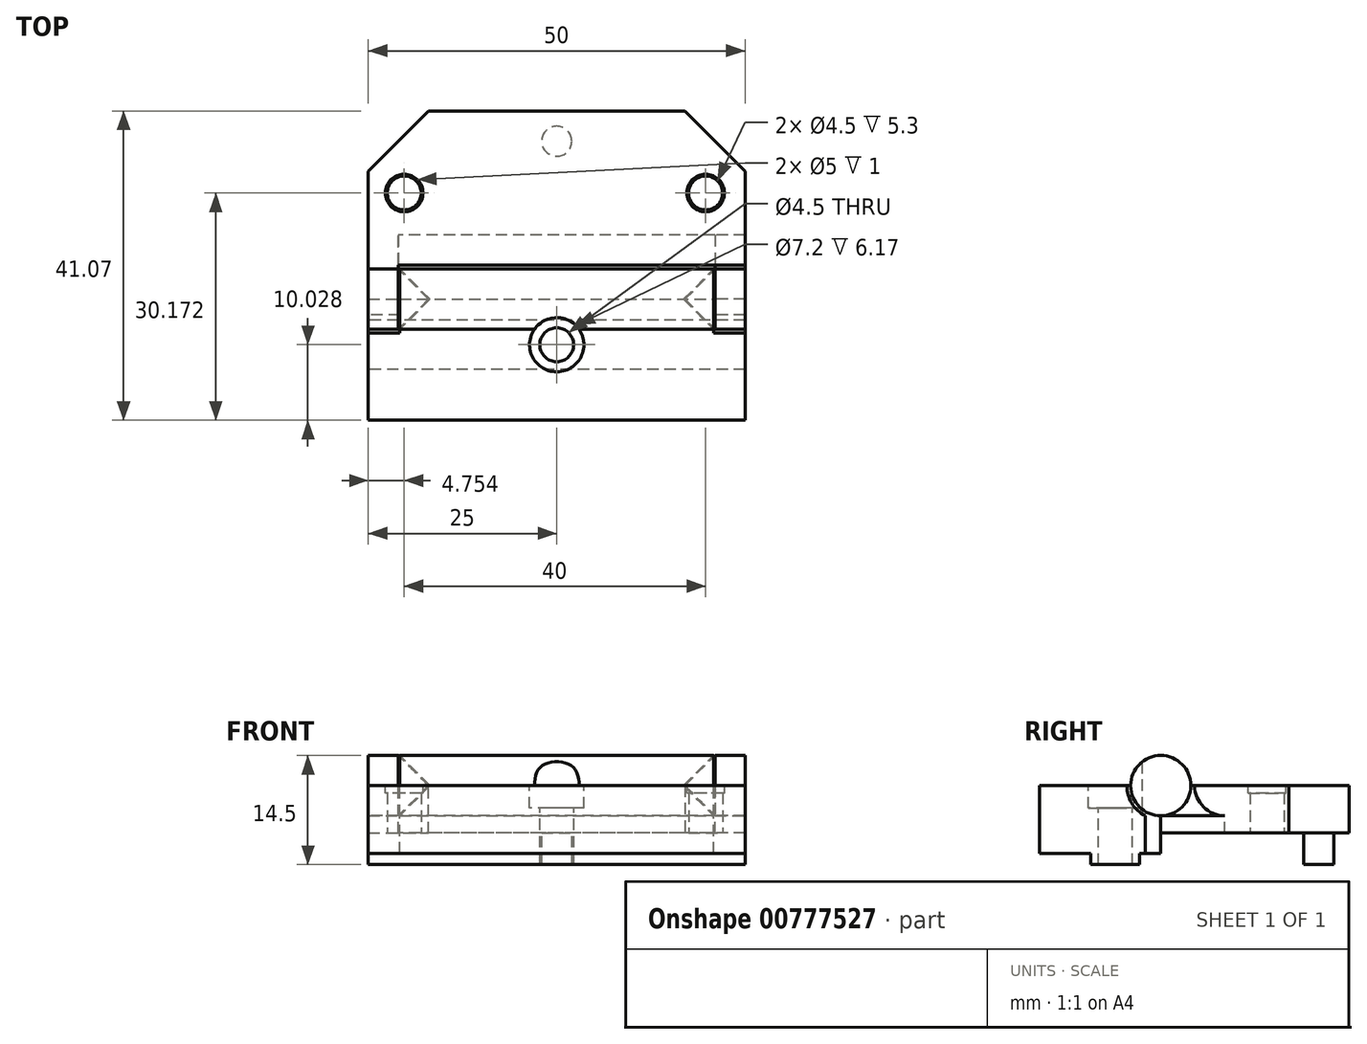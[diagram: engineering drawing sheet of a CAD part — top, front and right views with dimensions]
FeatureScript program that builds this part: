
annotation { "Feature Type Name" : "Feature", "Feature Type Description" : "" }
export const myFeature = defineFeature(function(context is Context, id is Id, definition is map)
    precondition{}
    {
        {
            var Q0;
            Q0=qCreatedBy(makeId("Top.planeOp"),FACE);
            var sketch = newSketch(context, id + "F0", { "sketchPlane" : qUnion([Q0])});
            skLineSegment(sketch, "E0", {"start": v(0, 0) * mm, "end": v(-16.82, 0) * mm});
            skLineSegment(sketch, "E1", {"start": v(-16.82, 0) * mm, "end": v(-20.82, 4) * mm});
            skLineSegment(sketch, "E2", {"start": v(-20.82, 4) * mm, "end": v(0, 4) * mm});
            skLineSegment(sketch, "E3", {"start": v(0, 4) * mm, "end": v(0, 0) * mm});
            skLineSegment(sketch, "E4", {"start": v(-17, 0) * mm, "end": v(-21, 4) * mm});
            skLineSegment(sketch, "E5", {"start": v(-21, 4) * mm, "end": v(-25, 4) * mm});
            skLineSegment(sketch, "E6", {"start": v(-25, 4) * mm, "end": v(-25, 0) * mm});
            skLineSegment(sketch, "E7", {"start": v(-25, 0) * mm, "end": v(-17, 0) * mm});
            skLineSegment(sketch, "E8.MirrorCS", {"start": v(21, 4) * mm, "end": v(25, 4) * mm});
            skLineSegment(sketch, "E9.MirrorCS", {"start": v(17, 0) * mm, "end": v(21, 4) * mm});
            skLineSegment(sketch, "E10.MirrorCS", {"start": v(25, 0) * mm, "end": v(17, 0) * mm});
            skLineSegment(sketch, "E11.MirrorCS", {"start": v(25, 4) * mm, "end": v(25, 0) * mm});
            skLineSegment(sketch, "E12.MirrorCS", {"start": v(16.82, 0) * mm, "end": v(20.82, 4) * mm});
            skLineSegment(sketch, "E13.MirrorCS", {"start": v(20.82, 4) * mm, "end": v(0, 4) * mm});
            skLineSegment(sketch, "E14.MirrorCS", {"start": v(0, 0) * mm, "end": v(16.82, 0) * mm});
            skSolve(sketch);
        }
        {
            var Q0;
            Q0=makeQuery(id+"F0.imprint","IMPRINT",FACE,{"disambiguationData":[TD([[makeQuery(id+"F0.imprint","IMPRINT",EDGE,{"derivedFrom":sQuery(id+"F0.wireOp",EDGE,"E4")}),1.0]])]});
            var Q1;
            Q1=makeQuery(id+"F0.imprint","IMPRINT",FACE,{"disambiguationData":[TD([[makeQuery(id+"F0.imprint","IMPRINT",EDGE,{"derivedFrom":sQuery(id+"F0.wireOp",EDGE,"E0")}),-1.0]])]});
            var Q2;
            Q2=makeQuery(id+"F0.imprint","IMPRINT",FACE,{"disambiguationData":[TD([[makeQuery(id+"F0.imprint","IMPRINT",EDGE,{"derivedFrom":sQuery(id+"F0.wireOp",EDGE,"E3")}),1.0]])]});
            var Q3;
            Q3=makeQuery(id+"F0.imprint","IMPRINT",FACE,{"disambiguationData":[TD([[makeQuery(id+"F0.imprint","IMPRINT",EDGE,{"derivedFrom":sQuery(id+"F0.wireOp",EDGE,"E8.MirrorCS")}),-1.0]])]});
            var Q4;
            Q4=sQuery(id+"F0.wireOp",EDGE,"E0");
            revolve(context, id + "F1", {"entities" : qUnion([Q0, Q1, Q2, Q3]), "axis" : qUnion([Q4]), "revolveType" : RevolveType.FULL});
        }
        {
            var Q0;
            Q0=qCreatedBy(makeId("Front.planeOp"),FACE);
            cPlane(context, id + "F2", {"entities" : qUnion([Q0]), "cplaneType" : CPlaneType.OFFSET, "offset" : 25 * mm, "width" : 150 * mm, "height" : 150 * mm});
        }
        {
            var Q0;
            Q0=qCreatedBy(makeId("Front.planeOp"),FACE);
            cPlane(context, id + "F3", {"entities" : qUnion([Q0]), "cplaneType" : CPlaneType.OFFSET, "offset" : 25 * mm, "oppositeDirection" : true, "width" : 150 * mm, "height" : 150 * mm});
        }
        {
            var Q0;
            Q0=qCreatedBy(id+"F2.planeOp",FACE);
            var sketch = newSketch(context, id + "F4", { "sketchPlane" : qUnion([Q0])});
            skLineSegment(sketch, "E15", {"start": v(20.82, -4) * mm, "end": v(-20.82, -4) * mm});
            skLineSegment(sketch, "E16", {"start": v(-20.82, 4) * mm, "end": v(20.82, 4) * mm});
            skLineSegment(sketch, "E17.0", {"start": v(-20.82, 4) * mm, "end": v(-20.82, -4) * mm});
            skLineSegment(sketch, "E18.0", {"start": v(20.82, 4) * mm, "end": v(20.82, -4) * mm});
            skSolve(sketch);
        }
        {
            var Q0;
            Q0=qSketchRegion(id+"F4",true);
            var Q1;
            Q1=makeQuery(id+"F1.opRevolve","SWEPT_FACE",FACE,{"disambiguationData":[OSD([sQuery(id+"F0.wireOp",EDGE,"E2"),sQuery(id+"F0.wireOp",EDGE,"E13.MirrorCS")])]});
            extrude(context, id + "F5", {"entities" : qUnion([Q0]), "operationType" : NewBodyOperationType.ADD, "endBound" : BoundingType.UP_TO_SURFACE, "oppositeDirection" : true, "endBoundEntityFace" : qUnion([Q1]), "depth" : 25 * mm});
        }
        {
            var Q0;
            Q0=qCreatedBy(id+"F3.planeOp",FACE);
            var sketch = newSketch(context, id + "F6", { "sketchPlane" : qUnion([Q0])});
            skLineSegment(sketch, "E19", {"start": v(25, -4) * mm, "end": v(21, -4) * mm});
            skLineSegment(sketch, "E20", {"start": v(21, 4) * mm, "end": v(25, 4) * mm});
            skLineSegment(sketch, "E21", {"start": v(-21, -4) * mm, "end": v(-25, -4) * mm});
            skLineSegment(sketch, "E22", {"start": v(-25, 4) * mm, "end": v(-21, 4) * mm});
            skLineSegment(sketch, "E23.0", {"start": v(-21, 4) * mm, "end": v(-21, -4) * mm});
            skLineSegment(sketch, "E24.0", {"start": v(-25, 4) * mm, "end": v(-25, -4) * mm});
            skLineSegment(sketch, "E25.0", {"start": v(21, 4) * mm, "end": v(21, -4) * mm});
            skLineSegment(sketch, "E26.0", {"start": v(25, 4) * mm, "end": v(25, -4) * mm});
            skSolve(sketch);
        }
        {
            var Q0;
            Q0=makeQuery(id+"F6.imprint","IMPRINT",FACE,{"disambiguationData":[TD([[makeQuery(id+"F6.imprint","IMPRINT",EDGE,{"derivedFrom":sQuery(id+"F6.wireOp",EDGE,"E19")}),-1.0]])]});
            var Q1;
            Q1=makeQuery(id+"F6.imprint","IMPRINT",FACE,{"disambiguationData":[TD([[makeQuery(id+"F6.imprint","IMPRINT",EDGE,{"derivedFrom":sQuery(id+"F6.wireOp",EDGE,"E21")}),-1.0]])]});
            extrude(context, id + "F7", {"entities" : qUnion([Q0, Q1]), "operationType" : NewBodyOperationType.ADD, "endBound" : BoundingType.UP_TO_NEXT, "depth" : 25 * mm, "offsetDistance" : 25 * mm});
        }
        {
            var Q0;
            Q0=makeQuery(id+"F7.opExtrude","SWEPT_FACE",FACE,{"disambiguationData":[OSD([sQuery(id+"F6.wireOp",EDGE,"E23.0")])]});
            var Q1;
            Q1=makeQuery(id+"F7.opExtrude","SWEPT_FACE",FACE,{"disambiguationData":[OSD([sQuery(id+"F6.wireOp",EDGE,"E25.0")])]});
            var Q2;
            Q2=makeQuery(id+"F1.opRevolve","SWEPT_BODY",BODY,{"disambiguationData":[OSD([sQuery(id+"F0.wireOp",EDGE,"E8.MirrorCS"),sQuery(id+"F0.wireOp",EDGE,"E9.MirrorCS"),sQuery(id+"F0.wireOp",EDGE,"E11.MirrorCS"),sQuery(id+"F0.wireOp",EDGE,"E10.MirrorCS")])]});
            extrude(context, id + "F8", {"entities" : qUnion([Q0]), "endBound" : BoundingType.UP_TO_SURFACE, "depth" : 6 * mm, "endBoundEntityFace" : qUnion([Q1]), "endBoundEntityBody" : qUnion([Q2]), "offsetDistance" : 25 * mm});
        }
        {
            var Q0;
            Q0=makeQuery(id+"F8.opExtrude","CAP_FACE",FACE,{"disambiguationData":[OSD([sQuery(id+"F6.wireOp",EDGE,"E23.0")])],"isStart":true});
            var sketch = newSketch(context, id + "F9", { "sketchPlane" : qUnion([Q0])});
            skArc(sketch, "E27.0", {"start": v(0, -4) * mm, "mid": v(-4, 0) * mm, "end": v(0, 4) * mm});
            skLineSegment(sketch, "E28", {"start": v(-4.25, 4) * mm, "end": v(-4.25, -4) * mm, "construction": true});
            skArc(sketch, "E29.MirrorCS", {"start": v(-8.5, -4) * mm, "mid": v(-4.5, 0) * mm, "end": v(-8.5, 4) * mm});
            skSolve(sketch);
        }
        {
            var Q0;
            {var subQ0=sQuery(id+"F9.wireOp",EDGE,"E27.0");Q0=makeQuery(id+"F9.imprint","IMPRINT",FACE,{"disambiguationData":[TD([[makeQuery(id+"F9.imprint","IMPRINT",EDGE,{"derivedFrom":subQ0}),1.0]])]});}
            extrude(context, id + "F10", {"entities" : qUnion([Q0]), "operationType" : NewBodyOperationType.REMOVE, "endBound" : BoundingType.THROUGH_ALL, "oppositeDirection" : true, "depth" : 25 * mm, "offsetDistance" : 25 * mm});
        }
        {
            var Q0;
            Q0=makeQuery(id+"F7.opExtrude","SWEPT_FACE",FACE,{"disambiguationData":[OSD([sQuery(id+"F6.wireOp",EDGE,"E23.0")])]});
            var sketch = newSketch(context, id + "F11", { "sketchPlane" : qUnion([Q0])});
            skLineSegment(sketch, "E30", {"start": v(25, 0) * mm, "end": v(4, 0) * mm});
            skSolve(sketch);
        }
        {
            var Q0;
            Q0=makeQuery(id+"F1.opRevolve","SWEPT_BODY",BODY,{"disambiguationData":[OSD([sQuery(id+"F0.wireOp",EDGE,"E8.MirrorCS"),sQuery(id+"F0.wireOp",EDGE,"E9.MirrorCS"),sQuery(id+"F0.wireOp",EDGE,"E11.MirrorCS"),sQuery(id+"F0.wireOp",EDGE,"E10.MirrorCS")])]});
            var Q1;
            Q1=makeQuery(id+"F8.opExtrude","SWEPT_BODY",BODY,{"disambiguationData":[OSD([sQuery(id+"F6.wireOp",EDGE,"E23.0")])]});
            var Q2;
            Q2=makeQuery(id+"F1.opRevolve","SWEPT_BODY",BODY,{"disambiguationData":[OSD([sQuery(id+"F0.wireOp",EDGE,"E4"),sQuery(id+"F0.wireOp",EDGE,"E5"),sQuery(id+"F0.wireOp",EDGE,"E6"),sQuery(id+"F0.wireOp",EDGE,"E7")])]});
            booleanBodies(context, id + "F12", {"operationType" : BooleanOperationType.UNION, "tools" : qUnion([Q0, Q1, Q2])});
        }
        {
            var Q0;
            Q0=makeQuery(id+"F5.opExtrude","SWEPT_FACE",FACE,{"disambiguationData":[OSD([sQuery(id+"F4.wireOp",EDGE,"E18.0")])]});
            var sketch = newSketch(context, id + "F13", { "sketchPlane" : qUnion([Q0])});
            skLineSegment(sketch, "E31", {"start": v(-25, 0) * mm, "end": v(-4, 0) * mm});
            skArc(sketch, "E32.0", {"start": v(-4.5, 0) * mm, "mid": v(-3.18, -3.18) * mm, "end": v(0, -4.5) * mm});
            skSolve(sketch);
        }
        {
            var Q0;
            {var subQ0=sQuery(id+"F11.wireOp",EDGE,"E30");Q0=makeQuery(id+"F11.imprint","IMPRINT",FACE,{"disambiguationData":[TD([[makeQuery(id+"F11.imprint","IMPRINT",EDGE,{"derivedFrom":subQ0}),-1.0]])]});}
            var Q1;
            Q1=makeQuery(id+"F7.boolean.opBoolean","MERGE",FACE,{"derivedFrom":[makeQuery(id+"F1.opRevolve","SWEPT_FACE",FACE,{"disambiguationData":[OSD([sQuery(id+"F0.wireOp",EDGE,"E6")])]}),makeQuery(id+"F7.opExtrude","SWEPT_FACE",FACE,{"disambiguationData":[OSD([sQuery(id+"F6.wireOp",EDGE,"E24.0")])]})]});
            var Q2;
            Q2=makeQuery(id+"F7.boolean.opBoolean","MERGE",FACE,{"derivedFrom":[makeQuery(id+"F1.opRevolve","SWEPT_FACE",FACE,{"disambiguationData":[OSD([sQuery(id+"F0.wireOp",EDGE,"E11.MirrorCS")])]}),makeQuery(id+"F7.opExtrude","SWEPT_FACE",FACE,{"disambiguationData":[OSD([sQuery(id+"F6.wireOp",EDGE,"E26.0")])]})]});
            extrude(context, id + "F14", {"entities" : qUnion([Q0]), "operationType" : NewBodyOperationType.REMOVE, "endBound" : BoundingType.UP_TO_SURFACE, "oppositeDirection" : true, "depth" : 25 * mm, "endBoundEntityFace" : qUnion([Q1]), "offsetDistance" : 25 * mm, "hasSecondDirection" : true, "secondDirectionBound" : SecondDirectionBoundingType.UP_TO_SURFACE, "secondDirectionOppositeDirection" : false, "secondDirectionDepth" : 25 * mm, "secondDirectionBoundEntityFace" : qUnion([Q2])});
        }
        {
            var Q0;
            {var subQ0=sQuery(id+"F13.wireOp",EDGE,"E31");Q0=makeQuery(id+"F13.imprint","IMPRINT",FACE,{"disambiguationData":[TD([[makeQuery(id+"F13.imprint","IMPRINT",EDGE,{"derivedFrom":subQ0}),1.0]])]});}
            extrude(context, id + "F15", {"entities" : qUnion([Q0]), "operationType" : NewBodyOperationType.REMOVE, "endBound" : BoundingType.UP_TO_NEXT, "oppositeDirection" : true, "depth" : 25 * mm, "offsetDistance" : 25 * mm});
        }
        {
            var Q0;
            {var subQ0=sQuery(id+"F13.wireOp",EDGE,"E31");var subQ1=sQuery(id+"F4.wireOp",EDGE,"E18.0");var subQ2=makeQuery(id+"F5.opExtrude","CAP_EDGE",EDGE,{"disambiguationData":[OSD([subQ1])],"isStart":true});var subQ3=makeQuery(id+"F13.imprint","INTERSECT",VERTEX,{"derivedFrom":[subQ2,subQ0]});Q0=makeQuery(id+"F13.imprint","IMPRINT",FACE,{"disambiguationData":[TD([[makeQuery(id+"F13.imprint","IMPRINT",EDGE,{"disambiguationData":[TD([[subQ3,-1.0]])],"derivedFrom":subQ0}),-1.0]])]});}
            var Q1;
            Q1=makeQuery(id+"F7.boolean.opBoolean","MERGE",FACE,{"derivedFrom":[makeQuery(id+"F1.opRevolve","SWEPT_FACE",FACE,{"disambiguationData":[OSD([sQuery(id+"F0.wireOp",EDGE,"E11.MirrorCS")])]}),makeQuery(id+"F7.opExtrude","SWEPT_FACE",FACE,{"disambiguationData":[OSD([sQuery(id+"F6.wireOp",EDGE,"E26.0")])]})]});
            var Q2;
            Q2=makeQuery(id+"F7.boolean.opBoolean","MERGE",FACE,{"derivedFrom":[makeQuery(id+"F1.opRevolve","SWEPT_FACE",FACE,{"disambiguationData":[OSD([sQuery(id+"F0.wireOp",EDGE,"E6")])]}),makeQuery(id+"F7.opExtrude","SWEPT_FACE",FACE,{"disambiguationData":[OSD([sQuery(id+"F6.wireOp",EDGE,"E24.0")])]})]});
            extrude(context, id + "F16", {"entities" : qUnion([Q0]), "operationType" : NewBodyOperationType.ADD, "endBound" : BoundingType.UP_TO_SURFACE, "depth" : 2.5 * mm, "endBoundEntityFace" : qUnion([Q1]), "offsetDistance" : 25 * mm, "hasSecondDirection" : true, "secondDirectionBound" : SecondDirectionBoundingType.UP_TO_SURFACE, "secondDirectionOppositeDirection" : true, "secondDirectionDepth" : 25 * mm, "secondDirectionBoundEntityFace" : qUnion([Q2])});
        }
        {
            var Q0;
            {var subQ0=sQuery(id+"F13.wireOp",EDGE,"E31");Q0=makeQuery(id+"F16.boolean.opBoolean","MERGE",FACE,{"derivedFrom":[makeQuery(id+"F15.boolean.opBoolean","COPY",FACE,{"derivedFrom":makeQuery(id+"F15.opExtrude","SWEPT_FACE",FACE,{"disambiguationData":[OSD([subQ0])]})}),makeQuery(id+"F16.opExtrude","SWEPT_FACE",FACE,{"disambiguationData":[OSD([subQ0])]})]});}
            var sketch = newSketch(context, id + "F17", { "sketchPlane" : qUnion([Q0])});
            skLineSegment(sketch, "E33.bottom", {"start": v(-19.55, 3.99) * mm, "end": v(2.5, 3.99) * mm, "construction": true});
            skLineSegment(sketch, "E33.top", {"start": v(-19.55, -16.07) * mm, "end": v(2.5, -16.07) * mm, "construction": true});
            skLineSegment(sketch, "E33.left", {"start": v(-19.55, 3.99) * mm, "end": v(-19.55, -16.07) * mm, "construction": true});
            skLineSegment(sketch, "E33.right", {"start": v(2.5, 3.99) * mm, "end": v(2.5, -16.07) * mm, "construction": true});
            skPoint(sketch, "E34.oppositeSnap0", {"position": v(25, -14.75) * mm});
            skLineSegment(sketch, "E34.bottom", {"start": v(-25, -25) * mm, "end": v(25, -25) * mm});
            skLineSegment(sketch, "E34.top", {"start": v(-25, -16.07) * mm, "end": v(25, -16.07) * mm});
            skLineSegment(sketch, "E34.left", {"start": v(-25, -25) * mm, "end": v(-25, -16.07) * mm});
            skLineSegment(sketch, "E34.right", {"start": v(25, -25) * mm, "end": v(25, -16.07) * mm});
            skLineSegment(sketch, "E35", {"start": v(-25, -6.04) * mm, "end": v(25, -6.04) * mm, "construction": true});
            skPoint(sketch, "E35.startSnap0", {"position": v(-19.55, -6.04) * mm});
            skCircle(sketch, "E36", {"center": v(0, -6.04) * mm, "radius": 2.25 * mm});
            skSolve(sketch);
        }
        {
            var Q0;
            Q0 = qSketchRegion(id + "F17", true);
            extrude(context, id + "F18", {"entities" : qUnion([Q0]), "operationType" : NewBodyOperationType.REMOVE, "oppositeDirection" : true, "depth" : 25 * mm, "offsetDistance" : 25 * mm});
        }
        {
            var Q0;
            {var subQ0=sQuery(id+"F4.wireOp",EDGE,"E15");Q0=makeQuery(id+"F16.boolean.opBoolean","MERGE",FACE,{"derivedFrom":[makeQuery(id+"F5.opExtrude","SWEPT_FACE",FACE,{"disambiguationData":[OSD([subQ0])]}),makeQuery(id+"F16.opExtrude","SWEPT_FACE",FACE,{"disambiguationData":[OSD([subQ0,sQuery(id+"F4.wireOp",EDGE,"E18.0")])]})]});}
            var sketch = newSketch(context, id + "F19", { "sketchPlane" : qUnion([Q0])});
            skLineSegment(sketch, "E37.bottom", {"start": v(-25, 16.07) * mm, "end": v(25, 16.07) * mm});
            skLineSegment(sketch, "E37.top", {"start": v(-25, 2.06) * mm, "end": v(-20.82, 2.06) * mm});
            skLineSegment(sketch, "E37.left", {"start": v(-25, 16.07) * mm, "end": v(-25, 2.06) * mm});
            skLineSegment(sketch, "E37.right", {"start": v(25, 16.07) * mm, "end": v(25, 2.06) * mm});
            skLineSegment(sketch, "E38.top", {"start": v(-20.82, 0) * mm, "end": v(20.82, 0) * mm});
            skLineSegment(sketch, "E38.left", {"start": v(-20.82, 2.06) * mm, "end": v(-20.82, 0) * mm});
            skLineSegment(sketch, "E38.right", {"start": v(20.82, 2.06) * mm, "end": v(20.82, 0) * mm});
            skLineSegment(sketch, "E39.trimOffspring", {"start": v(20.82, 2.06) * mm, "end": v(25, 2.06) * mm});
            skSolve(sketch);
        }
        {
            var Q0;
            Q0 = qSketchRegion(id + "F19", true);
            extrude(context, id + "F20", {"entities" : qUnion([Q0]), "operationType" : NewBodyOperationType.ADD, "depth" : 5 * mm, "offsetDistance" : 25 * mm});
        }
        {
            var Q0;
            {var subQ0=sQuery(id+"F13.wireOp",EDGE,"E31");Q0=makeQuery(id+"F16.boolean.opBoolean","MERGE",FACE,{"derivedFrom":[makeQuery(id+"F15.boolean.opBoolean","COPY",FACE,{"derivedFrom":makeQuery(id+"F15.opExtrude","SWEPT_FACE",FACE,{"disambiguationData":[OSD([subQ0])]})}),makeQuery(id+"F16.opExtrude","SWEPT_FACE",FACE,{"disambiguationData":[OSD([subQ0])]})]});}
            var sketch = newSketch(context, id + "F21", { "sketchPlane" : qUnion([Q0])});
            skCircle(sketch, "E40", {"center": v(0, -6.04) * mm, "radius": 2.25 * mm});
            skSolve(sketch);
        }
        {
            var Q0;
            Q0 = qSketchRegion(id + "F21", true);
            extrude(context, id + "F22", {"entities" : qUnion([Q0]), "operationType" : NewBodyOperationType.REMOVE, "oppositeDirection" : true, "depth" : 25 * mm, "offsetDistance" : 25 * mm});
        }
        {
            var Q0;
            {var subQ0=sQuery(id+"F13.wireOp",EDGE,"E31");Q0=makeQuery(id+"F16.boolean.opBoolean","MERGE",FACE,{"derivedFrom":[makeQuery(id+"F15.boolean.opBoolean","COPY",FACE,{"derivedFrom":makeQuery(id+"F15.opExtrude","SWEPT_FACE",FACE,{"disambiguationData":[OSD([subQ0])]})}),makeQuery(id+"F16.opExtrude","SWEPT_FACE",FACE,{"disambiguationData":[OSD([subQ0])]})]});}
            var sketch = newSketch(context, id + "F23", { "sketchPlane" : qUnion([Q0])});
            skCircle(sketch, "E41", {"center": v(0, -6.04) * mm, "radius": 3.6 * mm});
            skSolve(sketch);
        }
        {
            var Q0;
            Q0 = qSketchRegion(id + "F23", true);
            extrude(context, id + "F24", {"entities" : qUnion([Q0]), "operationType" : NewBodyOperationType.REMOVE, "oppositeDirection" : true, "depth" : 3 * mm, "offsetDistance" : 25 * mm, "hasSecondDirection" : true, "secondDirectionOppositeDirection" : false, "secondDirectionDepth" : 25 * mm});
        }
        {
            var Q0;
            Q0=makeQuery(id+"F20.opExtrude","CAP_FACE",FACE,{"disambiguationData":[OSD([sQuery(id+"F19.wireOp",EDGE,"E37.bottom"),sQuery(id+"F19.wireOp",EDGE,"E37.top"),sQuery(id+"F19.wireOp",EDGE,"E37.left"),sQuery(id+"F19.wireOp",EDGE,"E37.right"),sQuery(id+"F19.wireOp",EDGE,"E38.top"),sQuery(id+"F19.wireOp",EDGE,"E38.left"),sQuery(id+"F19.wireOp",EDGE,"E38.right"),sQuery(id+"F19.wireOp",EDGE,"E39.trimOffspring")])],"isStart":false});
            var sketch = newSketch(context, id + "F25", { "sketchPlane" : qUnion([Q0])});
            skLineSegment(sketch, "E42.bottom", {"start": v(25, 2.8) * mm, "end": v(-25, 2.8) * mm});
            skLineSegment(sketch, "E42.top", {"start": v(25, 9.3) * mm, "end": v(-25, 9.3) * mm});
            skLineSegment(sketch, "E42.left", {"start": v(25, 2.8) * mm, "end": v(25, 9.3) * mm});
            skLineSegment(sketch, "E42.right", {"start": v(-25, 2.8) * mm, "end": v(-25, 9.3) * mm});
            skPoint(sketch, "E42.middle", {"position": v(0, 6.04) * mm});
            skCircle(sketch, "E43", {"center": v(0, 6.04) * mm, "radius": 2.25 * mm});
            skSolve(sketch);
        }
        {
            var Q0;
            Q0 = qSketchRegion(id + "F25", true);
            extrude(context, id + "F26", {"entities" : qUnion([Q0]), "operationType" : NewBodyOperationType.ADD, "depth" : 1.5 * mm, "offsetDistance" : 25 * mm});
        }
        {
            var Q0;
            {var subQ0=sQuery(id+"F6.wireOp",EDGE,"E21");Q0=makeQuery(id+"F12.opBoolean","MERGE",FACE,{"derivedFrom":[makeQuery(id+"F7.opExtrude","SWEPT_FACE",FACE,{"disambiguationData":[OSD([sQuery(id+"F6.wireOp",EDGE,"E19")])]}),makeQuery(id+"F7.opExtrude","SWEPT_FACE",FACE,{"disambiguationData":[OSD([subQ0])]}),makeQuery(id+"F8.opExtrude","SWEPT_FACE",FACE,{"disambiguationData":[OSD([subQ0,sQuery(id+"F6.wireOp",EDGE,"E23.0")])]})]});}
            var sketch = newSketch(context, id + "F27", { "sketchPlane" : qUnion([Q0])});
            skPoint(sketch, "E44.orphan", {"position": v(-0.25, -14.1) * mm});
            skLineSegment(sketch, "E45", {"start": v(-0.25, -14.1) * mm, "end": v(-20.25, -14.1) * mm, "construction": true});
            skLineSegment(sketch, "E46", {"start": v(-0.25, -14.1) * mm, "end": v(19.75, -14.1) * mm, "construction": true});
            skCircle(sketch, "E47", {"center": v(-20.25, -14.1) * mm, "radius": 2.25 * mm});
            skCircle(sketch, "E48", {"center": v(19.75, -14.1) * mm, "radius": 2.25 * mm});
            skSolve(sketch);
        }
        {
            var Q0;
            Q0 = qSketchRegion(id + "F27", true);
            extrude(context, id + "F28", {"entities" : qUnion([Q0]), "operationType" : NewBodyOperationType.REMOVE, "oppositeDirection" : true, "depth" : 25 * mm, "offsetDistance" : 25 * mm});
        }
        {
            var Q0;
            {var subQ0=sQuery(id+"F6.wireOp",EDGE,"E21");Q0=makeQuery(id+"F12.opBoolean","MERGE",FACE,{"derivedFrom":[makeQuery(id+"F7.opExtrude","SWEPT_FACE",FACE,{"disambiguationData":[OSD([sQuery(id+"F6.wireOp",EDGE,"E19")])]}),makeQuery(id+"F7.opExtrude","SWEPT_FACE",FACE,{"disambiguationData":[OSD([subQ0])]}),makeQuery(id+"F8.opExtrude","SWEPT_FACE",FACE,{"disambiguationData":[OSD([subQ0,sQuery(id+"F6.wireOp",EDGE,"E23.0")])]})]});}
            var sketch = newSketch(context, id + "F29", { "sketchPlane" : qUnion([Q0])});
            skLineSegment(sketch, "E49.bottom", {"start": v(-25, -25) * mm, "end": v(25, -25) * mm});
            skLineSegment(sketch, "E49.top", {"start": v(-21, -8.5) * mm, "end": v(21, -8.5) * mm});
            skLineSegment(sketch, "E49.left", {"start": v(-25, -25) * mm, "end": v(-25, -8.5) * mm});
            skLineSegment(sketch, "E49.right", {"start": v(25, -25) * mm, "end": v(25, -8.5) * mm});
            skLineSegment(sketch, "E50.top", {"start": v(25, 0) * mm, "end": v(21, 0) * mm});
            skLineSegment(sketch, "E50.left", {"start": v(25, -8.5) * mm, "end": v(25, 0) * mm});
            skLineSegment(sketch, "E50.right", {"start": v(21, -8.5) * mm, "end": v(21, 0) * mm});
            skLineSegment(sketch, "E51.top", {"start": v(-25, 0) * mm, "end": v(-21, 0) * mm});
            skLineSegment(sketch, "E51.left", {"start": v(-25, -8.5) * mm, "end": v(-25, 0) * mm});
            skLineSegment(sketch, "E51.right", {"start": v(-21, -8.5) * mm, "end": v(-21, 0) * mm});
            skSolve(sketch);
        }
        {
            var Q0;
            Q0 = qSketchRegion(id + "F29", true);
            extrude(context, id + "F30", {"entities" : qUnion([Q0]), "operationType" : NewBodyOperationType.ADD, "depth" : 2.3 * mm, "offsetDistance" : 25 * mm});
        }
        {
            var Q0;
            Q0=makeQuery(id+"F14.boolean.opBoolean","COPY",FACE,{"derivedFrom":makeQuery(id+"F14.opExtrude","SWEPT_FACE",FACE,{"disambiguationData":[OSD([sQuery(id+"F11.wireOp",EDGE,"E30")])]})});
            var sketch = newSketch(context, id + "F31", { "sketchPlane" : qUnion([Q0])});
            skCircle(sketch, "E52", {"center": v(-20.25, 14.1) * mm, "radius": 2.25 * mm});
            skCircle(sketch, "E53", {"center": v(19.75, 14.1) * mm, "radius": 2.25 * mm});
            skSolve(sketch);
        }
        {
            var Q0;
            Q0 = qSketchRegion(id + "F31", true);
            extrude(context, id + "F32", {"entities" : qUnion([Q0]), "operationType" : NewBodyOperationType.REMOVE, "oppositeDirection" : true, "depth" : 25 * mm, "offsetDistance" : 25 * mm});
        }
        {
            var Q0;
            Q0=makeQuery(id+"F30.boolean.opBoolean","MERGE",EDGE,{"derivedFrom":[makeQuery(id+"F7.opExtrude","CAP_EDGE",EDGE,{"disambiguationData":[OSD([sQuery(id+"F6.wireOp",EDGE,"E24.0")])],"isStart":true}),makeQuery(id+"F30.opExtrude","SWEPT_EDGE",EDGE,{"disambiguationData":[OSD([sQuery(id+"F29.wireOp",EDGE,"E49.bottom"),sQuery(id+"F29.wireOp",EDGE,"E49.left")])]})]});
            var Q1;
            Q1=makeQuery(id+"F30.boolean.opBoolean","MERGE",EDGE,{"derivedFrom":[makeQuery(id+"F7.opExtrude","CAP_EDGE",EDGE,{"disambiguationData":[OSD([sQuery(id+"F6.wireOp",EDGE,"E26.0")])],"isStart":true}),makeQuery(id+"F30.opExtrude","SWEPT_EDGE",EDGE,{"disambiguationData":[OSD([sQuery(id+"F29.wireOp",EDGE,"E49.bottom"),sQuery(id+"F29.wireOp",EDGE,"E49.right")])]})]});
            chamfer(context, id + "F33", {"entities" : qUnion([Q0, Q1]), "width" : 8 * mm, "tangentPropagation" : true});
        }
        {
            var Q0;
            Q0=makeQuery(id+"F30.opExtrude","CAP_FACE",FACE,{"disambiguationData":[OSD([sQuery(id+"F29.wireOp",EDGE,"E49.bottom"),sQuery(id+"F29.wireOp",EDGE,"E49.top"),sQuery(id+"F29.wireOp",EDGE,"E49.left"),sQuery(id+"F29.wireOp",EDGE,"E49.right"),sQuery(id+"F29.wireOp",EDGE,"E50.top"),sQuery(id+"F29.wireOp",EDGE,"E50.left"),sQuery(id+"F29.wireOp",EDGE,"E50.right"),sQuery(id+"F29.wireOp",EDGE,"E51.top"),sQuery(id+"F29.wireOp",EDGE,"E51.left"),sQuery(id+"F29.wireOp",EDGE,"E51.right")])],"isStart":false});
            var sketch = newSketch(context, id + "F34", { "sketchPlane" : qUnion([Q0])});
            skCircle(sketch, "E54", {"center": v(0, -20.97) * mm, "radius": 2 * mm});
            skLineSegment(sketch, "E55", {"start": v(0, -8.5) * mm, "end": v(0, -25) * mm, "construction": true});
            skSolve(sketch);
        }
        {
            var Q0;
            Q0 = qSketchRegion(id + "F34", true);
            extrude(context, id + "F35", {"entities" : qUnion([Q0]), "operationType" : NewBodyOperationType.ADD, "depth" : 4.2 * mm, "offsetDistance" : 25 * mm});
        }
        {
            var Q0;
            Q0=makeQuery(id+"F14.boolean.opBoolean","COPY",FACE,{"derivedFrom":makeQuery(id+"F14.opExtrude","SWEPT_FACE",FACE,{"disambiguationData":[OSD([sQuery(id+"F11.wireOp",EDGE,"E30")])]})});
            var sketch = newSketch(context, id + "F36", { "sketchPlane" : qUnion([Q0])});
            skCircle(sketch, "E56", {"center": v(-20.25, 14.1) * mm, "radius": 2.5 * mm});
            skCircle(sketch, "E57", {"center": v(19.75, 14.1) * mm, "radius": 2.5 * mm});
            skSolve(sketch);
        }
        {
            var Q0;
            Q0 = qSketchRegion(id + "F36", true);
            extrude(context, id + "F37", {"entities" : qUnion([Q0]), "operationType" : NewBodyOperationType.REMOVE, "oppositeDirection" : true, "depth" : 1 * mm, "offsetDistance" : 25 * mm});
        }
    });
